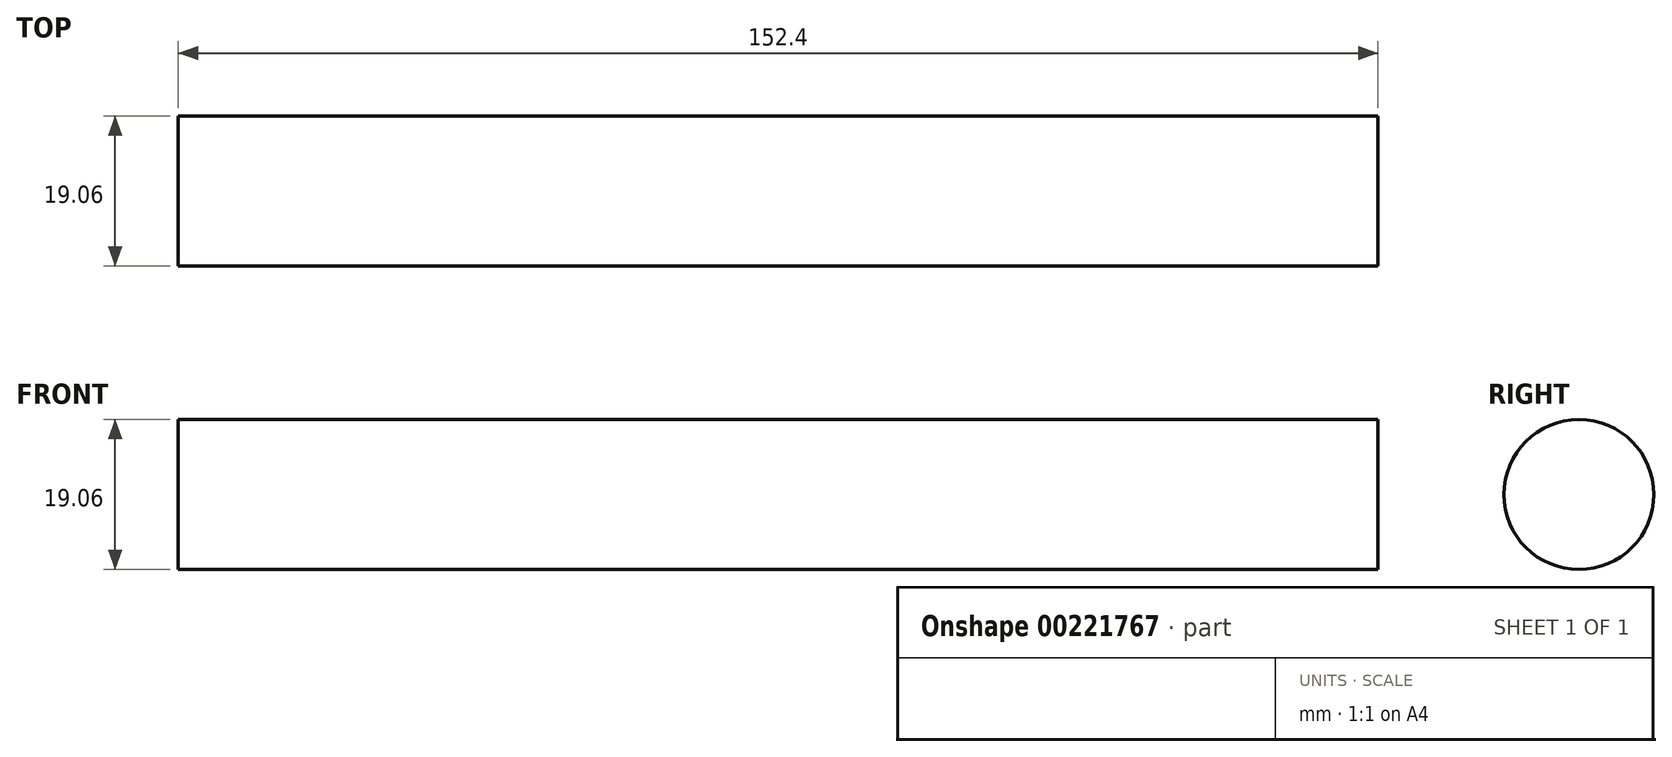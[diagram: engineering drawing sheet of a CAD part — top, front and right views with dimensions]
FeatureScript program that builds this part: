
annotation { "Feature Type Name" : "Feature", "Feature Type Description" : "" }
export const myFeature = defineFeature(function(context is Context, id is Id, definition is map)
    precondition{}
    {
        {
            var Q0;
            Q0=qCreatedBy(makeId("Right.planeOp"),FACE);
            var sketch = newSketch(context, id + "F0", { "sketchPlane" : qUnion([Q0])});
            skCircle(sketch, "E0", {"center": v(0, 0) * mm, "radius": 9.53 * mm});
            skSolve(sketch);
        }
        {
            var Q0;
            Q0 = qSketchRegion(id + "F0", true);
            extrude(context, id + "F1", {"entities" : qUnion([Q0]), "oppositeDirection" : true, "depth" : 152.4 * mm});
        }
    });
